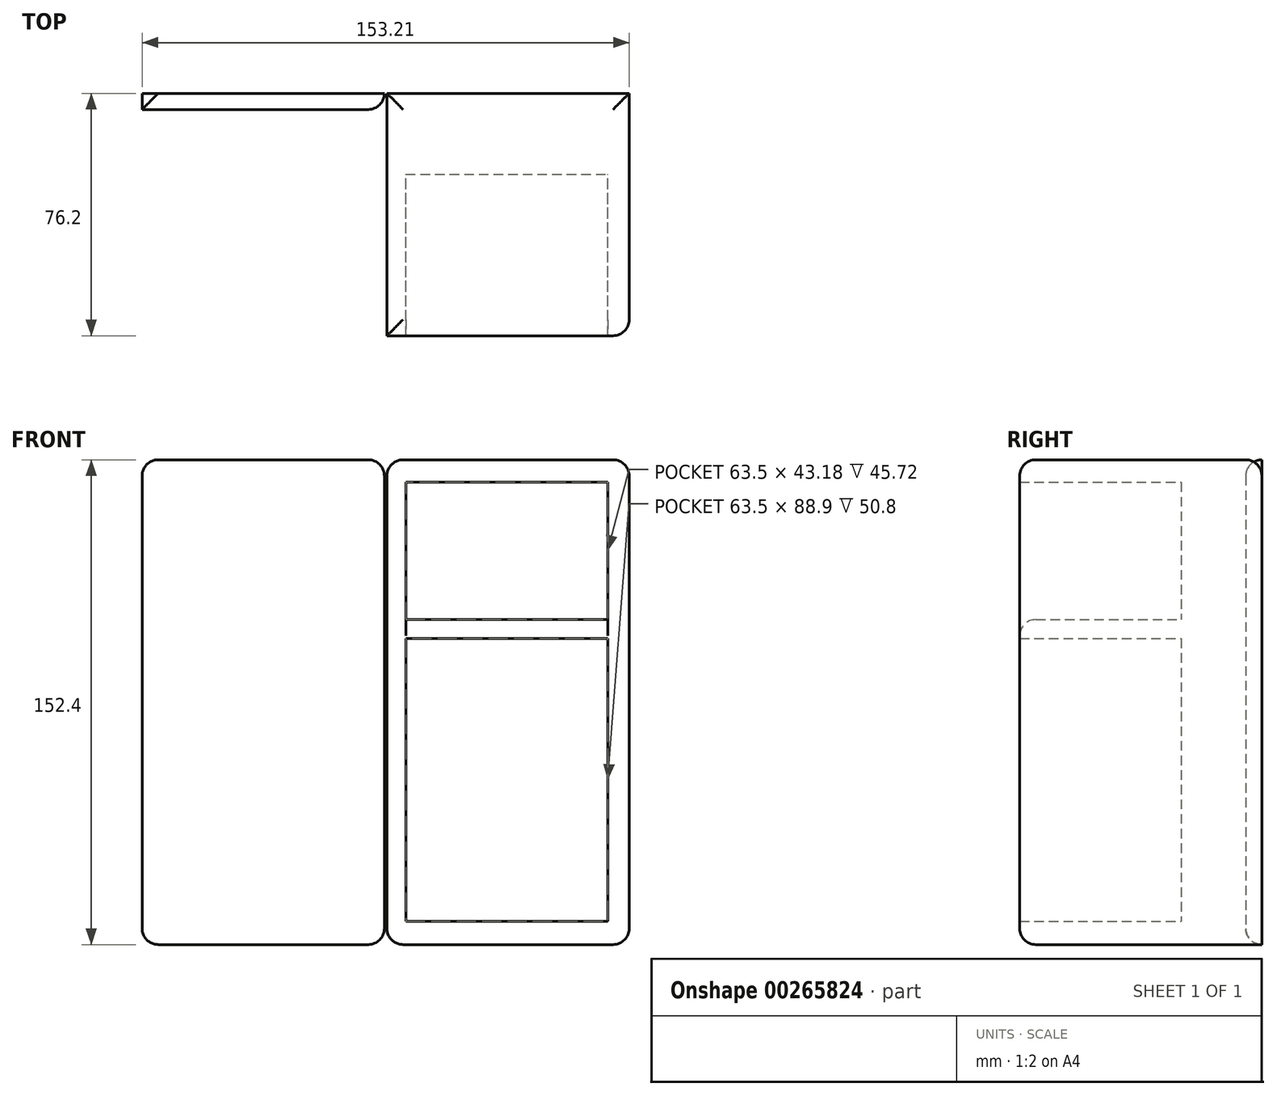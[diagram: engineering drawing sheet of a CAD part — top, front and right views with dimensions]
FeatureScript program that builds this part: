
annotation { "Feature Type Name" : "Feature", "Feature Type Description" : "" }
export const myFeature = defineFeature(function(context is Context, id is Id, definition is map)
    precondition{}
    {
        {
            var Q0;
            Q0=qCreatedBy(makeId("Front.planeOp"),FACE);
            var sketch = newSketch(context, id + "F0", { "sketchPlane" : qUnion([Q0])});
            skLineSegment(sketch, "E0.bottom", {"start": v(76.2, 75.66) * mm, "end": v(0, 75.66) * mm});
            skLineSegment(sketch, "E0.top", {"start": v(76.2, -76.74) * mm, "end": v(0, -76.74) * mm});
            skLineSegment(sketch, "E0.left", {"start": v(76.2, 75.66) * mm, "end": v(76.2, -76.74) * mm});
            skLineSegment(sketch, "E0.right", {"start": v(0, 75.66) * mm, "end": v(0, -76.74) * mm});
            skLineSegment(sketch, "E1.bottom", {"start": v(5.94, 68.58) * mm, "end": v(69.44, 68.58) * mm});
            skLineSegment(sketch, "E1.top", {"start": v(5.94, 25.4) * mm, "end": v(69.44, 25.4) * mm});
            skLineSegment(sketch, "E1.left", {"start": v(5.94, 68.58) * mm, "end": v(5.94, 25.4) * mm});
            skLineSegment(sketch, "E1.right", {"start": v(69.44, 68.58) * mm, "end": v(69.44, 25.4) * mm});
            skLineSegment(sketch, "E2.bottom", {"start": v(5.94, 19.46) * mm, "end": v(69.44, 19.46) * mm});
            skLineSegment(sketch, "E2.top", {"start": v(5.94, -69.44) * mm, "end": v(69.44, -69.44) * mm});
            skLineSegment(sketch, "E2.left", {"start": v(5.94, 19.46) * mm, "end": v(5.94, -69.44) * mm});
            skLineSegment(sketch, "E2.right", {"start": v(69.44, 19.46) * mm, "end": v(69.44, -69.44) * mm});
            skLineSegment(sketch, "E3.bottom", {"start": v(-77.01, 75.66) * mm, "end": v(-0.81, 75.66) * mm});
            skLineSegment(sketch, "E3.top", {"start": v(-77.01, -76.74) * mm, "end": v(-0.81, -76.74) * mm});
            skLineSegment(sketch, "E3.left", {"start": v(-77.01, 75.66) * mm, "end": v(-77.01, -76.74) * mm});
            skLineSegment(sketch, "E3.right", {"start": v(-0.81, 75.66) * mm, "end": v(-0.81, -76.74) * mm});
            skSolve(sketch);
        }
        {
            var Q0;
            Q0=makeQuery(id+"F0.imprint","IMPRINT",FACE,{"disambiguationData":[TD([[makeQuery(id+"F0.imprint","IMPRINT",EDGE,{"derivedFrom":sQuery(id+"F0.wireOp",EDGE,"E3.bottom")}),-1.0]])]});
            extrude(context, id + "F1", {"entities" : qUnion([Q0]), "depth" : 5.08 * mm});
        }
        {
            var Q0;
            Q0=makeQuery(id+"F0.imprint","IMPRINT",FACE,{"disambiguationData":[TD([[makeQuery(id+"F0.imprint","IMPRINT",EDGE,{"derivedFrom":sQuery(id+"F0.wireOp",EDGE,"E0.bottom")}),1.0]])]});
            extrude(context, id + "F2", {"entities" : qUnion([Q0]), "depth" : 76.2 * mm});
        }
        {
            var Q0;
            Q0=makeQuery(id+"F0.imprint","IMPRINT",FACE,{"disambiguationData":[TD([[makeQuery(id+"F0.imprint","IMPRINT",EDGE,{"derivedFrom":sQuery(id+"F0.wireOp",EDGE,"E1.bottom")}),-1.0]])]});
            var Q1;
            Q1=makeQuery(id+"F0.imprint","IMPRINT",FACE,{"disambiguationData":[TD([[makeQuery(id+"F0.imprint","IMPRINT",EDGE,{"derivedFrom":sQuery(id+"F0.wireOp",EDGE,"E2.bottom")}),-1.0]])]});
            extrude(context, id + "F3", {"entities" : qUnion([Q0, Q1]), "operationType" : NewBodyOperationType.ADD, "depth" : 25.4 * mm});
        }
        {
            var Q0;
            Q0=makeQuery(id+"F1.opExtrude","CAP_EDGE",EDGE,{"disambiguationData":[OSD([sQuery(id+"F0.wireOp",EDGE,"E3.right")])],"isStart":false});
            var Q1;
            Q1=makeQuery(id+"F1.opExtrude","CAP_EDGE",EDGE,{"disambiguationData":[OSD([sQuery(id+"F0.wireOp",EDGE,"E3.top")])],"isStart":false});
            var Q2;
            Q2=makeQuery(id+"F2.opExtrude","CAP_EDGE",EDGE,{"disambiguationData":[OSD([sQuery(id+"F0.wireOp",EDGE,"E0.left")])],"isStart":false});
            var Q3;
            Q3=makeQuery(id+"F2.opExtrude","CAP_EDGE",EDGE,{"disambiguationData":[OSD([sQuery(id+"F0.wireOp",EDGE,"E0.bottom")])],"isStart":true});
            var Q4;
            Q4=makeQuery(id+"F2.opExtrude","CAP_EDGE",EDGE,{"disambiguationData":[OSD([sQuery(id+"F0.wireOp",EDGE,"E1.top")])],"isStart":false});
            var Q5;
            Q5=makeQuery(id+"F2.opExtrude","CAP_EDGE",EDGE,{"disambiguationData":[OSD([sQuery(id+"F0.wireOp",EDGE,"E0.top")])],"isStart":false});
            var Q6;
            Q6=makeQuery(id+"F2.opExtrude","CAP_EDGE",EDGE,{"disambiguationData":[OSD([sQuery(id+"F0.wireOp",EDGE,"E0.bottom")])],"isStart":false});
            var Q7;
            Q7=makeQuery(id+"F2.opExtrude","SWEPT_EDGE",EDGE,{"disambiguationData":[OSD([sQuery(id+"F0.wireOp",EDGE,"E0.bottom"),sQuery(id+"F0.wireOp",EDGE,"E0.left")])]});
            var Q8;
            Q8=makeQuery(id+"F2.opExtrude","SWEPT_FACE",FACE,{"disambiguationData":[OSD([sQuery(id+"F0.wireOp",EDGE,"E0.bottom")])]});
            var Q9;
            Q9=makeQuery(id+"F2.opExtrude","SWEPT_EDGE",EDGE,{"disambiguationData":[OSD([sQuery(id+"F0.wireOp",EDGE,"E0.top"),sQuery(id+"F0.wireOp",EDGE,"E0.left")])]});
            var Q10;
            Q10=makeQuery(id+"F2.opExtrude","SWEPT_EDGE",EDGE,{"disambiguationData":[OSD([sQuery(id+"F0.wireOp",EDGE,"E0.top"),sQuery(id+"F0.wireOp",EDGE,"E0.right")])]});
            var Q11;
            Q11=makeQuery(id+"F1.opExtrude","SWEPT_EDGE",EDGE,{"disambiguationData":[OSD([sQuery(id+"F0.wireOp",EDGE,"E3.bottom"),sQuery(id+"F0.wireOp",EDGE,"E3.left")])]});
            var Q12;
            Q12=makeQuery(id+"F1.opExtrude","SWEPT_EDGE",EDGE,{"disambiguationData":[OSD([sQuery(id+"F0.wireOp",EDGE,"E3.top"),sQuery(id+"F0.wireOp",EDGE,"E3.left")])]});
            var Q13;
            Q13=makeQuery(id+"F1.opExtrude","SWEPT_EDGE",EDGE,{"disambiguationData":[OSD([sQuery(id+"F0.wireOp",EDGE,"E3.bottom"),sQuery(id+"F0.wireOp",EDGE,"E3.right")])]});
            var Q14;
            Q14=makeQuery(id+"F1.opExtrude","CAP_EDGE",EDGE,{"disambiguationData":[OSD([sQuery(id+"F0.wireOp",EDGE,"E3.bottom")])],"isStart":false});
            var Q15;
            Q15=makeQuery(id+"F1.opExtrude","SWEPT_EDGE",EDGE,{"disambiguationData":[OSD([sQuery(id+"F0.wireOp",EDGE,"E3.top"),sQuery(id+"F0.wireOp",EDGE,"E3.right")])]});
            fillet(context, id + "F4", {"entities" : qUnion([Q0, Q1, Q2, Q3, Q4, Q5, Q6, Q7, Q8, Q9, Q10, Q11, Q12, Q13, Q14, Q15]), "radius" : 5.08 * mm, "tangentPropagation" : true, "allowEdgeOverflow" : false});
        }
    });
